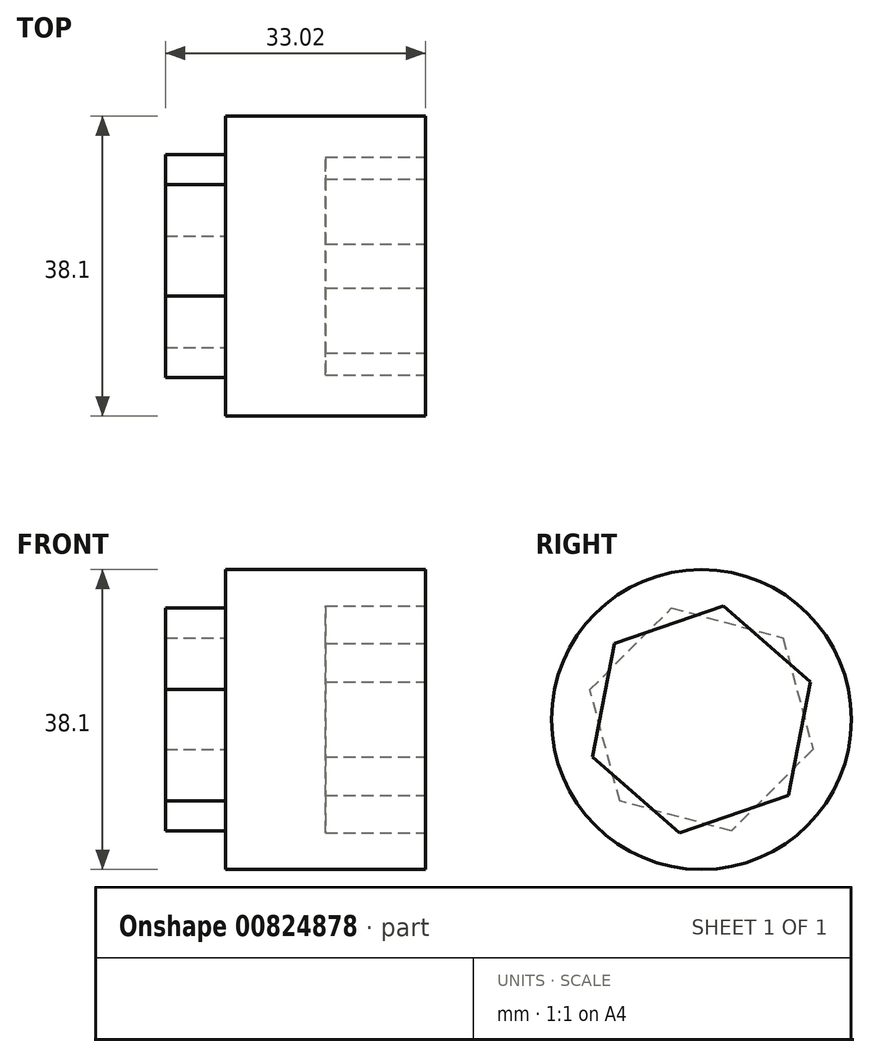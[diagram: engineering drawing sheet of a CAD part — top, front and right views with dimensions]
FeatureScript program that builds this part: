
annotation { "Feature Type Name" : "Feature", "Feature Type Description" : "" }
export const myFeature = defineFeature(function(context is Context, id is Id, definition is map)
    precondition{}
    {
        {
            var Q0;
            Q0=qCreatedBy(makeId("Right.planeOp"),FACE);
            var sketch = newSketch(context, id + "F0", { "sketchPlane" : qUnion([Q0])});
            skCircle(sketch, "E0", {"center": v(0, 0) * mm, "radius": 19.05 * mm});
            skSolve(sketch);
        }
        {
            var Q0;
            Q0 = qSketchRegion(id + "F0", true);
            extrude(context, id + "F1", {"entities" : qUnion([Q0]), "depth" : 25.4 * mm, "offsetDistance" : 25.4 * mm});
        }
        {
            var Q0;
            Q0=makeQuery(id+"F1.opExtrude","CAP_FACE",FACE,{"disambiguationData":[OSD([sQuery(id+"F0.wireOp",EDGE,"E0")])],"isStart":false});
            var sketch = newSketch(context, id + "F2", { "sketchPlane" : qUnion([Q0])});
            skCircle(sketch, "E1.cCircle", {"center": v(0, 0) * mm, "radius": 12.7 * mm, "construction": true});
            skLineSegment(sketch, "E1.0", {"start": v(2.8, 14.4) * mm, "end": v(13.87, 4.77) * mm});
            skLineSegment(sketch, "E1.1", {"start": v(13.87, 4.77) * mm, "end": v(11.06, -9.63) * mm});
            skLineSegment(sketch, "E1.2", {"start": v(11.06, -9.63) * mm, "end": v(-2.8, -14.4) * mm});
            skLineSegment(sketch, "E1.3", {"start": v(-2.8, -14.4) * mm, "end": v(-13.87, -4.77) * mm});
            skLineSegment(sketch, "E1.4", {"start": v(-13.87, -4.77) * mm, "end": v(-11.06, 9.63) * mm});
            skLineSegment(sketch, "E1.5", {"start": v(-11.06, 9.63) * mm, "end": v(2.8, 14.4) * mm});
            skPoint(sketch, "E1.0.midPoint", {"position": v(8.34, 9.58) * mm});
            skSolve(sketch);
        }
        {
            var Q0;
            Q0=makeQuery(id+"F2.imprint","IMPRINT",FACE,{"disambiguationData":[TD([[makeQuery(id+"F2.imprint","IMPRINT",EDGE,{"derivedFrom":sQuery(id+"F2.wireOp",EDGE,"E1.0")}),-1.0]])]});
            var Q1;
            Q1 = qSketchRegion(id + "F0", true);
            extrude(context, id + "F3", {"entities" : qUnion([Q0, Q1]), "operationType" : NewBodyOperationType.REMOVE, "oppositeDirection" : true, "depth" : 12.7 * mm, "offsetDistance" : 25.4 * mm});
        }
        {
            var Q0;
            Q0=qCreatedBy(makeId("Right.planeOp"),FACE);
            var sketch = newSketch(context, id + "F4", { "sketchPlane" : qUnion([Q0])});
            skCircle(sketch, "E2.cCircle", {"center": v(0, 0) * mm, "radius": 12.7 * mm, "construction": true});
            skLineSegment(sketch, "E2.0", {"start": v(14.17, -3.8) * mm, "end": v(3.8, -14.17) * mm});
            skLineSegment(sketch, "E2.1", {"start": v(3.8, -14.17) * mm, "end": v(-10.37, -10.37) * mm});
            skLineSegment(sketch, "E2.2", {"start": v(-10.37, -10.37) * mm, "end": v(-14.17, 3.8) * mm});
            skLineSegment(sketch, "E2.3", {"start": v(-14.17, 3.8) * mm, "end": v(-3.8, 14.17) * mm});
            skLineSegment(sketch, "E2.4", {"start": v(-3.8, 14.17) * mm, "end": v(10.37, 10.37) * mm});
            skLineSegment(sketch, "E2.5", {"start": v(10.37, 10.37) * mm, "end": v(14.17, -3.8) * mm});
            skPoint(sketch, "E2.0.midPoint", {"position": v(8.98, -8.98) * mm});
            skSolve(sketch);
        }
        {
            var Q0;
            Q0=makeQuery(id+"F4.imprint","IMPRINT",FACE,{"disambiguationData":[TD([[makeQuery(id+"F4.imprint","IMPRINT",EDGE,{"derivedFrom":sQuery(id+"F4.wireOp",EDGE,"E2.0")}),-1.0]])]});
            extrude(context, id + "F5", {"entities" : qUnion([Q0]), "operationType" : NewBodyOperationType.ADD, "oppositeDirection" : true, "depth" : 7.62 * mm, "offsetDistance" : 25.4 * mm});
        }
    });
